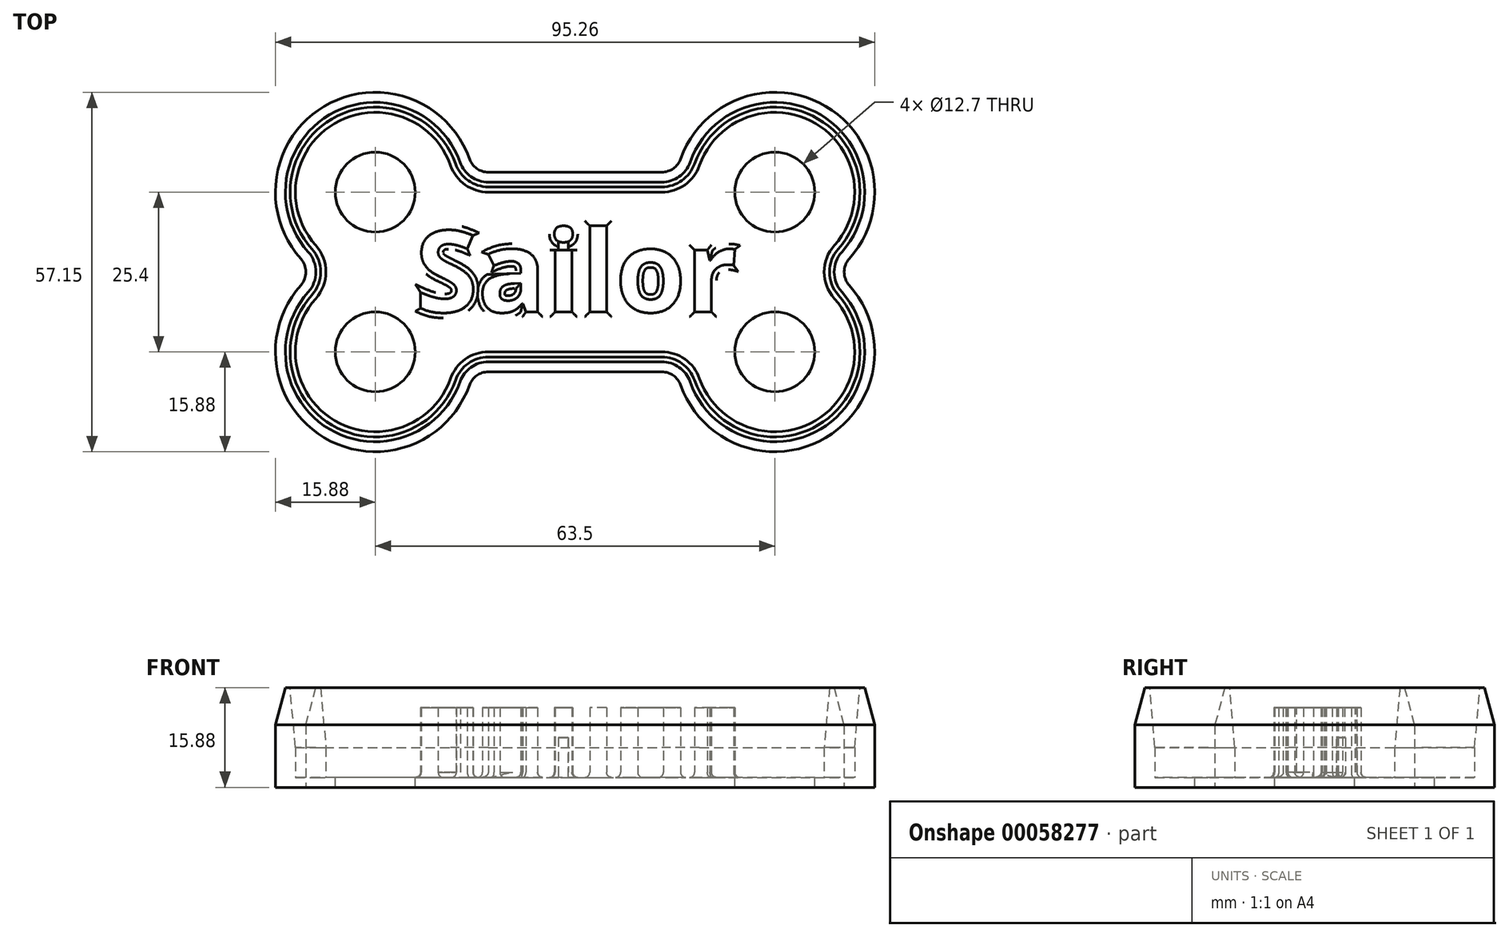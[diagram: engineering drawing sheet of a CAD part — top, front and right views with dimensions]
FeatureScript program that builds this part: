
annotation { "Feature Type Name" : "Feature", "Feature Type Description" : "" }
export const myFeature = defineFeature(function(context is Context, id is Id, definition is map)
    precondition{}
    {
        {
            var Q0;
            Q0=qCreatedBy(makeId("Top.planeOp"),FACE);
            var sketch = newSketch(context, id + "F0", { "sketchPlane" : qUnion([Q0])});
            skText(sketch, "E0", { "text": "Sailor", "fontName": "OpenSans-Bold.ttf"});
            const initialGuessF0  = {"E0": [0, 0, 1, 0, 0.01298]};
            skSetInitialGuess(sketch, initialGuessF0);
            skSolve(sketch);
        }
        {
            var Q0;
            Q0=qSketchRegion(id+"F0",true);
            extrude(context, id + "F1", {"entities" : qUnion([Q0]), "depth" : 12.7 * mm});
        }
        {
            var Q0;
            Q0=qCreatedBy(makeId("Top.planeOp"),FACE);
            var sketch = newSketch(context, id + "F2", { "sketchPlane" : qUnion([Q0])});
            skLineSegment(sketch, "E1.bottom", {"start": v(11.61, 19.05) * mm, "end": v(39.19, 19.05) * mm});
            skLineSegment(sketch, "E1.top", {"start": v(11.61, -6.35) * mm, "end": v(39.19, -6.35) * mm});
            skArc(sketch, "E2", {"start": v(5.62, 23.28) * mm, "mid": v(-12.82, 29.98) * mm, "end": v(-15.82, 10.58) * mm});
            skArc(sketch, "E3", {"start": v(-15.82, 2.12) * mm, "mid": v(-12.82, -17.28) * mm, "end": v(5.62, -10.58) * mm});
            skArc(sketch, "E4", {"start": v(66.62, 10.58) * mm, "mid": v(63.62, 29.98) * mm, "end": v(45.18, 23.28) * mm});
            skArc(sketch, "E5", {"start": v(45.18, -10.58) * mm, "mid": v(63.62, -17.28) * mm, "end": v(66.62, 2.12) * mm});
            skPoint(sketch, "E6.visualSharp", {"position": v(-6.35, 6.35) * mm});
            skArc(sketch, "E6.filletArc", {"start": v(-15.82, 2.12) * mm, "mid": v(-14.2, 6.35) * mm, "end": v(-15.82, 10.58) * mm});
            skPoint(sketch, "E7.visualSharp", {"position": v(57.15, 6.35) * mm});
            skArc(sketch, "E7.filletArc", {"start": v(66.62, 10.58) * mm, "mid": v(65, 6.35) * mm, "end": v(66.62, 2.12) * mm});
            skPoint(sketch, "E8.visualSharp", {"position": v(44.45, 19.05) * mm});
            skArc(sketch, "E8.filletArc", {"start": v(39.19, 19.05) * mm, "mid": v(42.86, 20.22) * mm, "end": v(45.18, 23.28) * mm});
            skPoint(sketch, "E9.visualSharp", {"position": v(6.35, 19.05) * mm});
            skArc(sketch, "E9.filletArc", {"start": v(5.62, 23.28) * mm, "mid": v(7.94, 20.22) * mm, "end": v(11.61, 19.05) * mm});
            skPoint(sketch, "E10.visualSharp", {"position": v(6.35, -6.35) * mm});
            skArc(sketch, "E10.filletArc", {"start": v(11.61, -6.35) * mm, "mid": v(7.94, -7.52) * mm, "end": v(5.62, -10.58) * mm});
            skPoint(sketch, "E11.visualSharp", {"position": v(44.45, -6.35) * mm});
            skArc(sketch, "E11.filletArc", {"start": v(45.18, -10.58) * mm, "mid": v(42.86, -7.52) * mm, "end": v(39.19, -6.35) * mm});
            skArc(sketch, "E12.0", {"start": v(8.62, 24.34) * mm, "mid": v(9.78, 22.8) * mm, "end": v(11.61, 22.23) * mm});
            skArc(sketch, "E12.1", {"start": v(42.18, -11.64) * mm, "mid": v(65.24, -20) * mm, "end": v(68.98, 4.23) * mm});
            skArc(sketch, "E12.2", {"start": v(68.98, 8.47) * mm, "mid": v(68.17, 6.35) * mm, "end": v(68.98, 4.23) * mm});
            skArc(sketch, "E12.3", {"start": v(68.98, 8.47) * mm, "mid": v(65.24, 32.7) * mm, "end": v(42.18, 24.34) * mm});
            skArc(sketch, "E12.4", {"start": v(39.19, 22.23) * mm, "mid": v(41.02, 22.8) * mm, "end": v(42.18, 24.34) * mm});
            skArc(sketch, "E12.5", {"start": v(42.18, -11.64) * mm, "mid": v(41.02, -10.1) * mm, "end": v(39.19, -9.52) * mm});
            skLineSegment(sketch, "E12.6", {"start": v(11.61, 22.22) * mm, "end": v(39.19, 22.23) * mm});
            skLineSegment(sketch, "E12.7", {"start": v(11.61, -9.53) * mm, "end": v(39.19, -9.52) * mm});
            skArc(sketch, "E12.8", {"start": v(11.61, -9.53) * mm, "mid": v(9.78, -10.1) * mm, "end": v(8.62, -11.64) * mm});
            skArc(sketch, "E12.9", {"start": v(-18.18, 4.23) * mm, "mid": v(-14.44, -20) * mm, "end": v(8.62, -11.64) * mm});
            skArc(sketch, "E12.10", {"start": v(-18.18, 4.23) * mm, "mid": v(-17.37, 6.35) * mm, "end": v(-18.18, 8.47) * mm});
            skArc(sketch, "E12.11", {"start": v(8.62, 24.34) * mm, "mid": v(-14.44, 32.7) * mm, "end": v(-18.18, 8.47) * mm});
            skSolve(sketch);
        }
        {
            var Q0;
            Q0=qSketchRegion(id+"F2",true);
            extrude(context, id + "F3", {"entities" : qUnion([Q0]), "depth" : 15.88 * mm});
        }
        {
            var Q0;
            Q0=makeQuery(id+"F3.opExtrude","CAP_EDGE",EDGE,{"disambiguationData":[OSD([sQuery(id+"F2.wireOp",EDGE,"E2")])],"isStart":false});
            chamfer(context, id + "F4", {"entities" : qUnion([Q0]), "chamferType" : ChamferType.OFFSET_ANGLE, "width" : 9.52 * mm, "oppositeDirection" : false, "angle" : 5 * degree, "tangentPropagation" : true});
        }
        {
            var Q0;
            Q0=makeQuery(id+"F3.opExtrude","CAP_EDGE",EDGE,{"disambiguationData":[OSD([sQuery(id+"F2.wireOp",EDGE,"E12.11")])],"isStart":false});
            chamfer(context, id + "F5", {"entities" : qUnion([Q0]), "chamferType" : ChamferType.OFFSET_ANGLE, "width" : 1.59 * mm, "oppositeDirection" : false, "angle" : 75 * degree, "tangentPropagation" : true});
        }
        {
            var Q0;
            Q0=qCreatedBy(makeId("Top.planeOp"),FACE);
            var sketch = newSketch(context, id + "F6", { "sketchPlane" : qUnion([Q0])});
            skArc(sketch, "E13.0", {"start": v(-18.18, 8.47) * mm, "mid": v(-14.44, 32.7) * mm, "end": v(8.62, 24.34) * mm});
            skArc(sketch, "E14.0", {"start": v(8.62, 24.34) * mm, "mid": v(9.78, 22.8) * mm, "end": v(11.61, 22.23) * mm});
            skLineSegment(sketch, "E15.0", {"start": v(11.61, 22.22) * mm, "end": v(39.19, 22.23) * mm});
            skArc(sketch, "E16.0", {"start": v(39.19, 22.23) * mm, "mid": v(41.02, 22.8) * mm, "end": v(42.18, 24.34) * mm});
            skArc(sketch, "E17.0", {"start": v(42.18, 24.34) * mm, "mid": v(65.24, 32.7) * mm, "end": v(68.98, 8.47) * mm});
            skArc(sketch, "E18.0", {"start": v(68.98, 8.47) * mm, "mid": v(68.17, 6.35) * mm, "end": v(68.98, 4.23) * mm});
            skArc(sketch, "E19.0", {"start": v(68.98, 4.23) * mm, "mid": v(65.24, -20) * mm, "end": v(42.18, -11.64) * mm});
            skArc(sketch, "E20.0", {"start": v(42.18, -11.64) * mm, "mid": v(41.02, -10.1) * mm, "end": v(39.19, -9.52) * mm});
            skLineSegment(sketch, "E21.0", {"start": v(39.19, -9.52) * mm, "end": v(11.61, -9.53) * mm});
            skArc(sketch, "E22.0", {"start": v(11.61, -9.53) * mm, "mid": v(9.78, -10.1) * mm, "end": v(8.62, -11.64) * mm});
            skArc(sketch, "E23.0", {"start": v(8.62, -11.64) * mm, "mid": v(-14.44, -20) * mm, "end": v(-18.18, 4.23) * mm});
            skArc(sketch, "E24.0", {"start": v(-18.18, 4.23) * mm, "mid": v(-17.37, 6.35) * mm, "end": v(-18.18, 8.47) * mm});
            skSolve(sketch);
        }
        {
            var Q0;
            Q0=qSketchRegion(id+"F6",true);
            extrude(context, id + "F7", {"entities" : qUnion([Q0]), "operationType" : NewBodyOperationType.ADD, "depth" : 1.59 * mm});
        }
        {
            var Q0;
            Q0=makeQuery(id+"F7.boolean.opBoolean","SPLIT",FACE,{"disambiguationData":[TD([makeQuery(id+"F1.opExtrude","SWEPT_FACE",FACE,{"disambiguationData":[OSD([sQuery(id+"F0.wireOp",EDGE,"E0.sketch_text.stroke-0")])]})])],"derivedFrom":makeQuery(id+"F7.opExtrude","CAP_FACE",FACE,{"disambiguationData":[OSD([sQuery(id+"F6.wireOp",EDGE,"E13.0"),sQuery(id+"F6.wireOp",EDGE,"E14.0"),sQuery(id+"F6.wireOp",EDGE,"E15.0"),sQuery(id+"F6.wireOp",EDGE,"E16.0"),sQuery(id+"F6.wireOp",EDGE,"E17.0"),sQuery(id+"F6.wireOp",EDGE,"E18.0"),sQuery(id+"F6.wireOp",EDGE,"E19.0"),sQuery(id+"F6.wireOp",EDGE,"E20.0"),sQuery(id+"F6.wireOp",EDGE,"E21.0"),sQuery(id+"F6.wireOp",EDGE,"E22.0"),sQuery(id+"F6.wireOp",EDGE,"E23.0"),sQuery(id+"F6.wireOp",EDGE,"E24.0")])],"isStart":false})});
            var sketch = newSketch(context, id + "F8", { "sketchPlane" : qUnion([Q0])});
            skLineSegment(sketch, "E25", {"start": v(22.73, 11.85) * mm, "end": v(22.73, 9.14) * mm});
            skLineSegment(sketch, "E26", {"start": v(22.73, 9.14) * mm, "end": v(24.32, 9.14) * mm});
            skLineSegment(sketch, "E27", {"start": v(24.32, 9.14) * mm, "end": v(24.32, 11.85) * mm});
            skLineSegment(sketch, "E28", {"start": v(24.32, 11.85) * mm, "end": v(22.73, 11.85) * mm});
            skSolve(sketch);
        }
        {
            var Q0;
            Q0=qSketchRegion(id+"F8",true);
            extrude(context, id + "F9", {"entities" : qUnion([Q0]), "operationType" : NewBodyOperationType.ADD, "depth" : 6.35 * mm});
        }
        {
            var Q0;
            Q0=makeQuery(id+"F7.boolean.opBoolean","INTERSECT",EDGE,{"derivedFrom":[makeQuery(id+"F1.opExtrude","SWEPT_FACE",FACE,{"disambiguationData":[OSD([sQuery(id+"F0.wireOp",EDGE,"E0.sketch_text.stroke-14")])]}),makeQuery(id+"F7.opExtrude","CAP_FACE",FACE,{"disambiguationData":[OSD([sQuery(id+"F6.wireOp",EDGE,"E13.0"),sQuery(id+"F6.wireOp",EDGE,"E14.0"),sQuery(id+"F6.wireOp",EDGE,"E15.0"),sQuery(id+"F6.wireOp",EDGE,"E16.0"),sQuery(id+"F6.wireOp",EDGE,"E17.0"),sQuery(id+"F6.wireOp",EDGE,"E18.0"),sQuery(id+"F6.wireOp",EDGE,"E19.0"),sQuery(id+"F6.wireOp",EDGE,"E20.0"),sQuery(id+"F6.wireOp",EDGE,"E21.0"),sQuery(id+"F6.wireOp",EDGE,"E22.0"),sQuery(id+"F6.wireOp",EDGE,"E23.0"),sQuery(id+"F6.wireOp",EDGE,"E24.0")])],"isStart":false})]});
            var Q1;
            Q1=makeQuery(id+"F7.boolean.opBoolean","INTERSECT",EDGE,{"derivedFrom":[makeQuery(id+"F1.opExtrude","SWEPT_FACE",FACE,{"disambiguationData":[OSD([sQuery(id+"F0.wireOp",EDGE,"E0.sketch_text.stroke-7")])]}),makeQuery(id+"F7.opExtrude","CAP_FACE",FACE,{"disambiguationData":[OSD([sQuery(id+"F6.wireOp",EDGE,"E13.0"),sQuery(id+"F6.wireOp",EDGE,"E14.0"),sQuery(id+"F6.wireOp",EDGE,"E15.0"),sQuery(id+"F6.wireOp",EDGE,"E16.0"),sQuery(id+"F6.wireOp",EDGE,"E17.0"),sQuery(id+"F6.wireOp",EDGE,"E18.0"),sQuery(id+"F6.wireOp",EDGE,"E19.0"),sQuery(id+"F6.wireOp",EDGE,"E20.0"),sQuery(id+"F6.wireOp",EDGE,"E21.0"),sQuery(id+"F6.wireOp",EDGE,"E22.0"),sQuery(id+"F6.wireOp",EDGE,"E23.0"),sQuery(id+"F6.wireOp",EDGE,"E24.0")])],"isStart":false})]});
            var Q2;
            Q2=makeQuery(id+"F7.boolean.opBoolean","INTERSECT",EDGE,{"derivedFrom":[makeQuery(id+"F1.opExtrude","SWEPT_FACE",FACE,{"disambiguationData":[OSD([sQuery(id+"F0.wireOp",EDGE,"E0.sketch_text.stroke-3")])]}),makeQuery(id+"F7.opExtrude","CAP_FACE",FACE,{"disambiguationData":[OSD([sQuery(id+"F6.wireOp",EDGE,"E13.0"),sQuery(id+"F6.wireOp",EDGE,"E14.0"),sQuery(id+"F6.wireOp",EDGE,"E15.0"),sQuery(id+"F6.wireOp",EDGE,"E16.0"),sQuery(id+"F6.wireOp",EDGE,"E17.0"),sQuery(id+"F6.wireOp",EDGE,"E18.0"),sQuery(id+"F6.wireOp",EDGE,"E19.0"),sQuery(id+"F6.wireOp",EDGE,"E20.0"),sQuery(id+"F6.wireOp",EDGE,"E21.0"),sQuery(id+"F6.wireOp",EDGE,"E22.0"),sQuery(id+"F6.wireOp",EDGE,"E23.0"),sQuery(id+"F6.wireOp",EDGE,"E24.0")])],"isStart":false})]});
            var Q3;
            Q3=makeQuery(id+"F7.boolean.opBoolean","INTERSECT",EDGE,{"derivedFrom":[makeQuery(id+"F1.opExtrude","SWEPT_FACE",FACE,{"disambiguationData":[OSD([sQuery(id+"F0.wireOp",EDGE,"E0.sketch_text.stroke-1")])]}),makeQuery(id+"F7.opExtrude","CAP_FACE",FACE,{"disambiguationData":[OSD([sQuery(id+"F6.wireOp",EDGE,"E13.0"),sQuery(id+"F6.wireOp",EDGE,"E14.0"),sQuery(id+"F6.wireOp",EDGE,"E15.0"),sQuery(id+"F6.wireOp",EDGE,"E16.0"),sQuery(id+"F6.wireOp",EDGE,"E17.0"),sQuery(id+"F6.wireOp",EDGE,"E18.0"),sQuery(id+"F6.wireOp",EDGE,"E19.0"),sQuery(id+"F6.wireOp",EDGE,"E20.0"),sQuery(id+"F6.wireOp",EDGE,"E21.0"),sQuery(id+"F6.wireOp",EDGE,"E22.0"),sQuery(id+"F6.wireOp",EDGE,"E23.0"),sQuery(id+"F6.wireOp",EDGE,"E24.0")])],"isStart":false})]});
            var Q4;
            Q4=makeQuery(id+"F7.boolean.opBoolean","INTERSECT",EDGE,{"derivedFrom":[makeQuery(id+"F1.opExtrude","SWEPT_FACE",FACE,{"disambiguationData":[OSD([sQuery(id+"F0.wireOp",EDGE,"E0.sketch_text.stroke-20")])]}),makeQuery(id+"F7.opExtrude","CAP_FACE",FACE,{"disambiguationData":[OSD([sQuery(id+"F6.wireOp",EDGE,"E13.0"),sQuery(id+"F6.wireOp",EDGE,"E14.0"),sQuery(id+"F6.wireOp",EDGE,"E15.0"),sQuery(id+"F6.wireOp",EDGE,"E16.0"),sQuery(id+"F6.wireOp",EDGE,"E17.0"),sQuery(id+"F6.wireOp",EDGE,"E18.0"),sQuery(id+"F6.wireOp",EDGE,"E19.0"),sQuery(id+"F6.wireOp",EDGE,"E20.0"),sQuery(id+"F6.wireOp",EDGE,"E21.0"),sQuery(id+"F6.wireOp",EDGE,"E22.0"),sQuery(id+"F6.wireOp",EDGE,"E23.0"),sQuery(id+"F6.wireOp",EDGE,"E24.0")])],"isStart":false})]});
            var Q5;
            Q5=makeQuery(id+"F7.boolean.opBoolean","INTERSECT",EDGE,{"derivedFrom":[makeQuery(id+"F1.opExtrude","SWEPT_FACE",FACE,{"disambiguationData":[OSD([sQuery(id+"F0.wireOp",EDGE,"E0.sketch_text.stroke-18")])]}),makeQuery(id+"F7.opExtrude","CAP_FACE",FACE,{"disambiguationData":[OSD([sQuery(id+"F6.wireOp",EDGE,"E13.0"),sQuery(id+"F6.wireOp",EDGE,"E14.0"),sQuery(id+"F6.wireOp",EDGE,"E15.0"),sQuery(id+"F6.wireOp",EDGE,"E16.0"),sQuery(id+"F6.wireOp",EDGE,"E17.0"),sQuery(id+"F6.wireOp",EDGE,"E18.0"),sQuery(id+"F6.wireOp",EDGE,"E19.0"),sQuery(id+"F6.wireOp",EDGE,"E20.0"),sQuery(id+"F6.wireOp",EDGE,"E21.0"),sQuery(id+"F6.wireOp",EDGE,"E22.0"),sQuery(id+"F6.wireOp",EDGE,"E23.0"),sQuery(id+"F6.wireOp",EDGE,"E24.0")])],"isStart":false})]});
            var Q6;
            Q6=makeQuery(id+"F7.boolean.opBoolean","INTERSECT",EDGE,{"derivedFrom":[makeQuery(id+"F1.opExtrude","SWEPT_FACE",FACE,{"disambiguationData":[OSD([sQuery(id+"F0.wireOp",EDGE,"E0.sketch_text.stroke-32")])]}),makeQuery(id+"F7.opExtrude","CAP_FACE",FACE,{"disambiguationData":[OSD([sQuery(id+"F6.wireOp",EDGE,"E13.0"),sQuery(id+"F6.wireOp",EDGE,"E14.0"),sQuery(id+"F6.wireOp",EDGE,"E15.0"),sQuery(id+"F6.wireOp",EDGE,"E16.0"),sQuery(id+"F6.wireOp",EDGE,"E17.0"),sQuery(id+"F6.wireOp",EDGE,"E18.0"),sQuery(id+"F6.wireOp",EDGE,"E19.0"),sQuery(id+"F6.wireOp",EDGE,"E20.0"),sQuery(id+"F6.wireOp",EDGE,"E21.0"),sQuery(id+"F6.wireOp",EDGE,"E22.0"),sQuery(id+"F6.wireOp",EDGE,"E23.0"),sQuery(id+"F6.wireOp",EDGE,"E24.0")])],"isStart":false})]});
            var Q7;
            Q7=makeQuery(id+"F7.boolean.opBoolean","INTERSECT",EDGE,{"derivedFrom":[makeQuery(id+"F1.opExtrude","SWEPT_FACE",FACE,{"disambiguationData":[OSD([sQuery(id+"F0.wireOp",EDGE,"E0.sketch_text.stroke-28")])]}),makeQuery(id+"F7.opExtrude","CAP_FACE",FACE,{"disambiguationData":[OSD([sQuery(id+"F6.wireOp",EDGE,"E13.0"),sQuery(id+"F6.wireOp",EDGE,"E14.0"),sQuery(id+"F6.wireOp",EDGE,"E15.0"),sQuery(id+"F6.wireOp",EDGE,"E16.0"),sQuery(id+"F6.wireOp",EDGE,"E17.0"),sQuery(id+"F6.wireOp",EDGE,"E18.0"),sQuery(id+"F6.wireOp",EDGE,"E19.0"),sQuery(id+"F6.wireOp",EDGE,"E20.0"),sQuery(id+"F6.wireOp",EDGE,"E21.0"),sQuery(id+"F6.wireOp",EDGE,"E22.0"),sQuery(id+"F6.wireOp",EDGE,"E23.0"),sQuery(id+"F6.wireOp",EDGE,"E24.0")])],"isStart":false})]});
            var Q8;
            Q8=makeQuery(id+"F7.boolean.opBoolean","INTERSECT",EDGE,{"derivedFrom":[makeQuery(id+"F1.opExtrude","SWEPT_FACE",FACE,{"disambiguationData":[OSD([sQuery(id+"F0.wireOp",EDGE,"E0.sketch_text.stroke-45")])]}),makeQuery(id+"F7.opExtrude","CAP_FACE",FACE,{"disambiguationData":[OSD([sQuery(id+"F6.wireOp",EDGE,"E13.0"),sQuery(id+"F6.wireOp",EDGE,"E14.0"),sQuery(id+"F6.wireOp",EDGE,"E15.0"),sQuery(id+"F6.wireOp",EDGE,"E16.0"),sQuery(id+"F6.wireOp",EDGE,"E17.0"),sQuery(id+"F6.wireOp",EDGE,"E18.0"),sQuery(id+"F6.wireOp",EDGE,"E19.0"),sQuery(id+"F6.wireOp",EDGE,"E20.0"),sQuery(id+"F6.wireOp",EDGE,"E21.0"),sQuery(id+"F6.wireOp",EDGE,"E22.0"),sQuery(id+"F6.wireOp",EDGE,"E23.0"),sQuery(id+"F6.wireOp",EDGE,"E24.0")])],"isStart":false})]});
            var Q9;
            Q9=makeQuery(id+"F7.boolean.opBoolean","INTERSECT",EDGE,{"derivedFrom":[makeQuery(id+"F1.opExtrude","SWEPT_FACE",FACE,{"disambiguationData":[OSD([sQuery(id+"F0.wireOp",EDGE,"E0.sketch_text.stroke-44")])]}),makeQuery(id+"F7.opExtrude","CAP_FACE",FACE,{"disambiguationData":[OSD([sQuery(id+"F6.wireOp",EDGE,"E13.0"),sQuery(id+"F6.wireOp",EDGE,"E14.0"),sQuery(id+"F6.wireOp",EDGE,"E15.0"),sQuery(id+"F6.wireOp",EDGE,"E16.0"),sQuery(id+"F6.wireOp",EDGE,"E17.0"),sQuery(id+"F6.wireOp",EDGE,"E18.0"),sQuery(id+"F6.wireOp",EDGE,"E19.0"),sQuery(id+"F6.wireOp",EDGE,"E20.0"),sQuery(id+"F6.wireOp",EDGE,"E21.0"),sQuery(id+"F6.wireOp",EDGE,"E22.0"),sQuery(id+"F6.wireOp",EDGE,"E23.0"),sQuery(id+"F6.wireOp",EDGE,"E24.0")])],"isStart":false})]});
            var Q10;
            Q10=makeQuery(id+"F7.boolean.opBoolean","INTERSECT",EDGE,{"derivedFrom":[makeQuery(id+"F1.opExtrude","SWEPT_FACE",FACE,{"disambiguationData":[OSD([sQuery(id+"F0.wireOp",EDGE,"E0.sketch_text.stroke-40")])]}),makeQuery(id+"F7.opExtrude","CAP_FACE",FACE,{"disambiguationData":[OSD([sQuery(id+"F6.wireOp",EDGE,"E13.0"),sQuery(id+"F6.wireOp",EDGE,"E14.0"),sQuery(id+"F6.wireOp",EDGE,"E15.0"),sQuery(id+"F6.wireOp",EDGE,"E16.0"),sQuery(id+"F6.wireOp",EDGE,"E17.0"),sQuery(id+"F6.wireOp",EDGE,"E18.0"),sQuery(id+"F6.wireOp",EDGE,"E19.0"),sQuery(id+"F6.wireOp",EDGE,"E20.0"),sQuery(id+"F6.wireOp",EDGE,"E21.0"),sQuery(id+"F6.wireOp",EDGE,"E22.0"),sQuery(id+"F6.wireOp",EDGE,"E23.0"),sQuery(id+"F6.wireOp",EDGE,"E24.0")])],"isStart":false})]});
            var Q11;
            Q11=makeQuery(id+"F7.boolean.opBoolean","INTERSECT",EDGE,{"derivedFrom":[makeQuery(id+"F1.opExtrude","SWEPT_FACE",FACE,{"disambiguationData":[OSD([sQuery(id+"F0.wireOp",EDGE,"E0.sketch_text.stroke-39")])]}),makeQuery(id+"F7.opExtrude","CAP_FACE",FACE,{"disambiguationData":[OSD([sQuery(id+"F6.wireOp",EDGE,"E13.0"),sQuery(id+"F6.wireOp",EDGE,"E14.0"),sQuery(id+"F6.wireOp",EDGE,"E15.0"),sQuery(id+"F6.wireOp",EDGE,"E16.0"),sQuery(id+"F6.wireOp",EDGE,"E17.0"),sQuery(id+"F6.wireOp",EDGE,"E18.0"),sQuery(id+"F6.wireOp",EDGE,"E19.0"),sQuery(id+"F6.wireOp",EDGE,"E20.0"),sQuery(id+"F6.wireOp",EDGE,"E21.0"),sQuery(id+"F6.wireOp",EDGE,"E22.0"),sQuery(id+"F6.wireOp",EDGE,"E23.0"),sQuery(id+"F6.wireOp",EDGE,"E24.0")])],"isStart":false})]});
            var Q12;
            Q12=makeQuery(id+"F7.boolean.opBoolean","INTERSECT",EDGE,{"derivedFrom":[makeQuery(id+"F1.opExtrude","SWEPT_FACE",FACE,{"disambiguationData":[OSD([sQuery(id+"F0.wireOp",EDGE,"E0.sketch_text.stroke-52")])]}),makeQuery(id+"F7.opExtrude","CAP_FACE",FACE,{"disambiguationData":[OSD([sQuery(id+"F6.wireOp",EDGE,"E13.0"),sQuery(id+"F6.wireOp",EDGE,"E14.0"),sQuery(id+"F6.wireOp",EDGE,"E15.0"),sQuery(id+"F6.wireOp",EDGE,"E16.0"),sQuery(id+"F6.wireOp",EDGE,"E17.0"),sQuery(id+"F6.wireOp",EDGE,"E18.0"),sQuery(id+"F6.wireOp",EDGE,"E19.0"),sQuery(id+"F6.wireOp",EDGE,"E20.0"),sQuery(id+"F6.wireOp",EDGE,"E21.0"),sQuery(id+"F6.wireOp",EDGE,"E22.0"),sQuery(id+"F6.wireOp",EDGE,"E23.0"),sQuery(id+"F6.wireOp",EDGE,"E24.0")])],"isStart":false})]});
            var Q13;
            Q13=makeQuery(id+"F7.boolean.opBoolean","INTERSECT",EDGE,{"derivedFrom":[makeQuery(id+"F1.opExtrude","SWEPT_FACE",FACE,{"disambiguationData":[OSD([sQuery(id+"F0.wireOp",EDGE,"E0.sketch_text.stroke-59")])]}),makeQuery(id+"F7.opExtrude","CAP_FACE",FACE,{"disambiguationData":[OSD([sQuery(id+"F6.wireOp",EDGE,"E13.0"),sQuery(id+"F6.wireOp",EDGE,"E14.0"),sQuery(id+"F6.wireOp",EDGE,"E15.0"),sQuery(id+"F6.wireOp",EDGE,"E16.0"),sQuery(id+"F6.wireOp",EDGE,"E17.0"),sQuery(id+"F6.wireOp",EDGE,"E18.0"),sQuery(id+"F6.wireOp",EDGE,"E19.0"),sQuery(id+"F6.wireOp",EDGE,"E20.0"),sQuery(id+"F6.wireOp",EDGE,"E21.0"),sQuery(id+"F6.wireOp",EDGE,"E22.0"),sQuery(id+"F6.wireOp",EDGE,"E23.0"),sQuery(id+"F6.wireOp",EDGE,"E24.0")])],"isStart":false})]});
            var Q14;
            Q14=makeQuery(id+"F7.boolean.opBoolean","INTERSECT",EDGE,{"derivedFrom":[makeQuery(id+"F1.opExtrude","SWEPT_FACE",FACE,{"disambiguationData":[OSD([sQuery(id+"F0.wireOp",EDGE,"E0.sketch_text.stroke-58")])]}),makeQuery(id+"F7.opExtrude","CAP_FACE",FACE,{"disambiguationData":[OSD([sQuery(id+"F6.wireOp",EDGE,"E13.0"),sQuery(id+"F6.wireOp",EDGE,"E14.0"),sQuery(id+"F6.wireOp",EDGE,"E15.0"),sQuery(id+"F6.wireOp",EDGE,"E16.0"),sQuery(id+"F6.wireOp",EDGE,"E17.0"),sQuery(id+"F6.wireOp",EDGE,"E18.0"),sQuery(id+"F6.wireOp",EDGE,"E19.0"),sQuery(id+"F6.wireOp",EDGE,"E20.0"),sQuery(id+"F6.wireOp",EDGE,"E21.0"),sQuery(id+"F6.wireOp",EDGE,"E22.0"),sQuery(id+"F6.wireOp",EDGE,"E23.0"),sQuery(id+"F6.wireOp",EDGE,"E24.0")])],"isStart":false})]});
            var Q15;
            Q15=makeQuery(id+"F7.boolean.opBoolean","INTERSECT",EDGE,{"derivedFrom":[makeQuery(id+"F1.opExtrude","SWEPT_FACE",FACE,{"disambiguationData":[OSD([sQuery(id+"F0.wireOp",EDGE,"E0.sketch_text.stroke-61")])]}),makeQuery(id+"F7.opExtrude","CAP_FACE",FACE,{"disambiguationData":[OSD([sQuery(id+"F6.wireOp",EDGE,"E13.0"),sQuery(id+"F6.wireOp",EDGE,"E14.0"),sQuery(id+"F6.wireOp",EDGE,"E15.0"),sQuery(id+"F6.wireOp",EDGE,"E16.0"),sQuery(id+"F6.wireOp",EDGE,"E17.0"),sQuery(id+"F6.wireOp",EDGE,"E18.0"),sQuery(id+"F6.wireOp",EDGE,"E19.0"),sQuery(id+"F6.wireOp",EDGE,"E20.0"),sQuery(id+"F6.wireOp",EDGE,"E21.0"),sQuery(id+"F6.wireOp",EDGE,"E22.0"),sQuery(id+"F6.wireOp",EDGE,"E23.0"),sQuery(id+"F6.wireOp",EDGE,"E24.0")])],"isStart":false})]});
            var Q16;
            Q16=makeQuery(id+"F7.boolean.opBoolean","INTERSECT",EDGE,{"derivedFrom":[makeQuery(id+"F1.opExtrude","SWEPT_FACE",FACE,{"disambiguationData":[OSD([sQuery(id+"F0.wireOp",EDGE,"E0.sketch_text.stroke-62")])]}),makeQuery(id+"F7.opExtrude","CAP_FACE",FACE,{"disambiguationData":[OSD([sQuery(id+"F6.wireOp",EDGE,"E13.0"),sQuery(id+"F6.wireOp",EDGE,"E14.0"),sQuery(id+"F6.wireOp",EDGE,"E15.0"),sQuery(id+"F6.wireOp",EDGE,"E16.0"),sQuery(id+"F6.wireOp",EDGE,"E17.0"),sQuery(id+"F6.wireOp",EDGE,"E18.0"),sQuery(id+"F6.wireOp",EDGE,"E19.0"),sQuery(id+"F6.wireOp",EDGE,"E20.0"),sQuery(id+"F6.wireOp",EDGE,"E21.0"),sQuery(id+"F6.wireOp",EDGE,"E22.0"),sQuery(id+"F6.wireOp",EDGE,"E23.0"),sQuery(id+"F6.wireOp",EDGE,"E24.0")])],"isStart":false})]});
            var Q17;
            Q17=makeQuery(id+"F7.boolean.opBoolean","INTERSECT",EDGE,{"derivedFrom":[makeQuery(id+"F1.opExtrude","SWEPT_FACE",FACE,{"disambiguationData":[OSD([sQuery(id+"F0.wireOp",EDGE,"E0.sketch_text.stroke-65")])]}),makeQuery(id+"F7.opExtrude","CAP_FACE",FACE,{"disambiguationData":[OSD([sQuery(id+"F6.wireOp",EDGE,"E13.0"),sQuery(id+"F6.wireOp",EDGE,"E14.0"),sQuery(id+"F6.wireOp",EDGE,"E15.0"),sQuery(id+"F6.wireOp",EDGE,"E16.0"),sQuery(id+"F6.wireOp",EDGE,"E17.0"),sQuery(id+"F6.wireOp",EDGE,"E18.0"),sQuery(id+"F6.wireOp",EDGE,"E19.0"),sQuery(id+"F6.wireOp",EDGE,"E20.0"),sQuery(id+"F6.wireOp",EDGE,"E21.0"),sQuery(id+"F6.wireOp",EDGE,"E22.0"),sQuery(id+"F6.wireOp",EDGE,"E23.0"),sQuery(id+"F6.wireOp",EDGE,"E24.0")])],"isStart":false})]});
            var Q18;
            Q18=makeQuery(id+"F7.boolean.opBoolean","INTERSECT",EDGE,{"derivedFrom":[makeQuery(id+"F1.opExtrude","SWEPT_FACE",FACE,{"disambiguationData":[OSD([sQuery(id+"F0.wireOp",EDGE,"E0.sketch_text.stroke-55")])]}),makeQuery(id+"F7.opExtrude","CAP_FACE",FACE,{"disambiguationData":[OSD([sQuery(id+"F6.wireOp",EDGE,"E13.0"),sQuery(id+"F6.wireOp",EDGE,"E14.0"),sQuery(id+"F6.wireOp",EDGE,"E15.0"),sQuery(id+"F6.wireOp",EDGE,"E16.0"),sQuery(id+"F6.wireOp",EDGE,"E17.0"),sQuery(id+"F6.wireOp",EDGE,"E18.0"),sQuery(id+"F6.wireOp",EDGE,"E19.0"),sQuery(id+"F6.wireOp",EDGE,"E20.0"),sQuery(id+"F6.wireOp",EDGE,"E21.0"),sQuery(id+"F6.wireOp",EDGE,"E22.0"),sQuery(id+"F6.wireOp",EDGE,"E23.0"),sQuery(id+"F6.wireOp",EDGE,"E24.0")])],"isStart":false})]});
            var Q19;
            Q19=makeQuery(id+"F7.boolean.opBoolean","INTERSECT",EDGE,{"derivedFrom":[makeQuery(id+"F1.opExtrude","SWEPT_FACE",FACE,{"disambiguationData":[OSD([sQuery(id+"F0.wireOp",EDGE,"E0.sketch_text.stroke-63")])]}),makeQuery(id+"F7.opExtrude","CAP_FACE",FACE,{"disambiguationData":[OSD([sQuery(id+"F6.wireOp",EDGE,"E13.0"),sQuery(id+"F6.wireOp",EDGE,"E14.0"),sQuery(id+"F6.wireOp",EDGE,"E15.0"),sQuery(id+"F6.wireOp",EDGE,"E16.0"),sQuery(id+"F6.wireOp",EDGE,"E17.0"),sQuery(id+"F6.wireOp",EDGE,"E18.0"),sQuery(id+"F6.wireOp",EDGE,"E19.0"),sQuery(id+"F6.wireOp",EDGE,"E20.0"),sQuery(id+"F6.wireOp",EDGE,"E21.0"),sQuery(id+"F6.wireOp",EDGE,"E22.0"),sQuery(id+"F6.wireOp",EDGE,"E23.0"),sQuery(id+"F6.wireOp",EDGE,"E24.0")])],"isStart":false})]});
            var Q20;
            Q20=makeQuery(id+"F7.boolean.opBoolean","INTERSECT",EDGE,{"derivedFrom":[makeQuery(id+"F1.opExtrude","SWEPT_FACE",FACE,{"disambiguationData":[OSD([sQuery(id+"F0.wireOp",EDGE,"E0.sketch_text.stroke-64")])]}),makeQuery(id+"F7.opExtrude","CAP_FACE",FACE,{"disambiguationData":[OSD([sQuery(id+"F6.wireOp",EDGE,"E13.0"),sQuery(id+"F6.wireOp",EDGE,"E14.0"),sQuery(id+"F6.wireOp",EDGE,"E15.0"),sQuery(id+"F6.wireOp",EDGE,"E16.0"),sQuery(id+"F6.wireOp",EDGE,"E17.0"),sQuery(id+"F6.wireOp",EDGE,"E18.0"),sQuery(id+"F6.wireOp",EDGE,"E19.0"),sQuery(id+"F6.wireOp",EDGE,"E20.0"),sQuery(id+"F6.wireOp",EDGE,"E21.0"),sQuery(id+"F6.wireOp",EDGE,"E22.0"),sQuery(id+"F6.wireOp",EDGE,"E23.0"),sQuery(id+"F6.wireOp",EDGE,"E24.0")])],"isStart":false})]});
            var Q21;
            Q21=makeQuery(id+"F7.boolean.opBoolean","INTERSECT",EDGE,{"derivedFrom":[makeQuery(id+"F1.opExtrude","SWEPT_FACE",FACE,{"disambiguationData":[OSD([sQuery(id+"F0.wireOp",EDGE,"E0.sketch_text.stroke-80")])]}),makeQuery(id+"F7.opExtrude","CAP_FACE",FACE,{"disambiguationData":[OSD([sQuery(id+"F6.wireOp",EDGE,"E13.0"),sQuery(id+"F6.wireOp",EDGE,"E14.0"),sQuery(id+"F6.wireOp",EDGE,"E15.0"),sQuery(id+"F6.wireOp",EDGE,"E16.0"),sQuery(id+"F6.wireOp",EDGE,"E17.0"),sQuery(id+"F6.wireOp",EDGE,"E18.0"),sQuery(id+"F6.wireOp",EDGE,"E19.0"),sQuery(id+"F6.wireOp",EDGE,"E20.0"),sQuery(id+"F6.wireOp",EDGE,"E21.0"),sQuery(id+"F6.wireOp",EDGE,"E22.0"),sQuery(id+"F6.wireOp",EDGE,"E23.0"),sQuery(id+"F6.wireOp",EDGE,"E24.0")])],"isStart":false})]});
            var Q22;
            Q22=makeQuery(id+"F7.boolean.opBoolean","INTERSECT",EDGE,{"derivedFrom":[makeQuery(id+"F1.opExtrude","SWEPT_FACE",FACE,{"disambiguationData":[OSD([sQuery(id+"F0.wireOp",EDGE,"E0.sketch_text.stroke-71")])]}),makeQuery(id+"F7.opExtrude","CAP_FACE",FACE,{"disambiguationData":[OSD([sQuery(id+"F6.wireOp",EDGE,"E13.0"),sQuery(id+"F6.wireOp",EDGE,"E14.0"),sQuery(id+"F6.wireOp",EDGE,"E15.0"),sQuery(id+"F6.wireOp",EDGE,"E16.0"),sQuery(id+"F6.wireOp",EDGE,"E17.0"),sQuery(id+"F6.wireOp",EDGE,"E18.0"),sQuery(id+"F6.wireOp",EDGE,"E19.0"),sQuery(id+"F6.wireOp",EDGE,"E20.0"),sQuery(id+"F6.wireOp",EDGE,"E21.0"),sQuery(id+"F6.wireOp",EDGE,"E22.0"),sQuery(id+"F6.wireOp",EDGE,"E23.0"),sQuery(id+"F6.wireOp",EDGE,"E24.0")])],"isStart":false})]});
            var Q23;
            Q23=makeQuery(id+"F7.boolean.opBoolean","INTERSECT",EDGE,{"derivedFrom":[makeQuery(id+"F1.opExtrude","SWEPT_FACE",FACE,{"disambiguationData":[OSD([sQuery(id+"F0.wireOp",EDGE,"E0.sketch_text.stroke-91")])]}),makeQuery(id+"F7.opExtrude","CAP_FACE",FACE,{"disambiguationData":[OSD([sQuery(id+"F6.wireOp",EDGE,"E13.0"),sQuery(id+"F6.wireOp",EDGE,"E14.0"),sQuery(id+"F6.wireOp",EDGE,"E15.0"),sQuery(id+"F6.wireOp",EDGE,"E16.0"),sQuery(id+"F6.wireOp",EDGE,"E17.0"),sQuery(id+"F6.wireOp",EDGE,"E18.0"),sQuery(id+"F6.wireOp",EDGE,"E19.0"),sQuery(id+"F6.wireOp",EDGE,"E20.0"),sQuery(id+"F6.wireOp",EDGE,"E21.0"),sQuery(id+"F6.wireOp",EDGE,"E22.0"),sQuery(id+"F6.wireOp",EDGE,"E23.0"),sQuery(id+"F6.wireOp",EDGE,"E24.0")])],"isStart":false})]});
            var Q24;
            Q24=makeQuery(id+"F7.boolean.opBoolean","INTERSECT",EDGE,{"derivedFrom":[makeQuery(id+"F1.opExtrude","SWEPT_FACE",FACE,{"disambiguationData":[OSD([sQuery(id+"F0.wireOp",EDGE,"E0.sketch_text.stroke-90")])]}),makeQuery(id+"F7.opExtrude","CAP_FACE",FACE,{"disambiguationData":[OSD([sQuery(id+"F6.wireOp",EDGE,"E13.0"),sQuery(id+"F6.wireOp",EDGE,"E14.0"),sQuery(id+"F6.wireOp",EDGE,"E15.0"),sQuery(id+"F6.wireOp",EDGE,"E16.0"),sQuery(id+"F6.wireOp",EDGE,"E17.0"),sQuery(id+"F6.wireOp",EDGE,"E18.0"),sQuery(id+"F6.wireOp",EDGE,"E19.0"),sQuery(id+"F6.wireOp",EDGE,"E20.0"),sQuery(id+"F6.wireOp",EDGE,"E21.0"),sQuery(id+"F6.wireOp",EDGE,"E22.0"),sQuery(id+"F6.wireOp",EDGE,"E23.0"),sQuery(id+"F6.wireOp",EDGE,"E24.0")])],"isStart":false})]});
            var Q25;
            Q25=makeQuery(id+"F7.boolean.opBoolean","INTERSECT",EDGE,{"derivedFrom":[makeQuery(id+"F1.opExtrude","SWEPT_FACE",FACE,{"disambiguationData":[OSD([sQuery(id+"F0.wireOp",EDGE,"E0.sketch_text.stroke-87")])]}),makeQuery(id+"F7.opExtrude","CAP_FACE",FACE,{"disambiguationData":[OSD([sQuery(id+"F6.wireOp",EDGE,"E13.0"),sQuery(id+"F6.wireOp",EDGE,"E14.0"),sQuery(id+"F6.wireOp",EDGE,"E15.0"),sQuery(id+"F6.wireOp",EDGE,"E16.0"),sQuery(id+"F6.wireOp",EDGE,"E17.0"),sQuery(id+"F6.wireOp",EDGE,"E18.0"),sQuery(id+"F6.wireOp",EDGE,"E19.0"),sQuery(id+"F6.wireOp",EDGE,"E20.0"),sQuery(id+"F6.wireOp",EDGE,"E21.0"),sQuery(id+"F6.wireOp",EDGE,"E22.0"),sQuery(id+"F6.wireOp",EDGE,"E23.0"),sQuery(id+"F6.wireOp",EDGE,"E24.0")])],"isStart":false})]});
            var Q26;
            Q26=makeQuery(id+"F7.boolean.opBoolean","INTERSECT",EDGE,{"derivedFrom":[makeQuery(id+"F1.opExtrude","SWEPT_FACE",FACE,{"disambiguationData":[OSD([sQuery(id+"F0.wireOp",EDGE,"E0.sketch_text.stroke-85")])]}),makeQuery(id+"F7.opExtrude","CAP_FACE",FACE,{"disambiguationData":[OSD([sQuery(id+"F6.wireOp",EDGE,"E13.0"),sQuery(id+"F6.wireOp",EDGE,"E14.0"),sQuery(id+"F6.wireOp",EDGE,"E15.0"),sQuery(id+"F6.wireOp",EDGE,"E16.0"),sQuery(id+"F6.wireOp",EDGE,"E17.0"),sQuery(id+"F6.wireOp",EDGE,"E18.0"),sQuery(id+"F6.wireOp",EDGE,"E19.0"),sQuery(id+"F6.wireOp",EDGE,"E20.0"),sQuery(id+"F6.wireOp",EDGE,"E21.0"),sQuery(id+"F6.wireOp",EDGE,"E22.0"),sQuery(id+"F6.wireOp",EDGE,"E23.0"),sQuery(id+"F6.wireOp",EDGE,"E24.0")])],"isStart":false})]});
            var Q27;
            Q27=makeQuery(id+"F7.boolean.opBoolean","INTERSECT",EDGE,{"derivedFrom":[makeQuery(id+"F1.opExtrude","SWEPT_FACE",FACE,{"disambiguationData":[OSD([sQuery(id+"F0.wireOp",EDGE,"E0.sketch_text.stroke-96")])]}),makeQuery(id+"F7.opExtrude","CAP_FACE",FACE,{"disambiguationData":[OSD([sQuery(id+"F6.wireOp",EDGE,"E13.0"),sQuery(id+"F6.wireOp",EDGE,"E14.0"),sQuery(id+"F6.wireOp",EDGE,"E15.0"),sQuery(id+"F6.wireOp",EDGE,"E16.0"),sQuery(id+"F6.wireOp",EDGE,"E17.0"),sQuery(id+"F6.wireOp",EDGE,"E18.0"),sQuery(id+"F6.wireOp",EDGE,"E19.0"),sQuery(id+"F6.wireOp",EDGE,"E20.0"),sQuery(id+"F6.wireOp",EDGE,"E21.0"),sQuery(id+"F6.wireOp",EDGE,"E22.0"),sQuery(id+"F6.wireOp",EDGE,"E23.0"),sQuery(id+"F6.wireOp",EDGE,"E24.0")])],"isStart":false})]});
            var Q28;
            Q28=makeQuery(id+"F7.boolean.opBoolean","INTERSECT",EDGE,{"derivedFrom":[makeQuery(id+"F1.opExtrude","SWEPT_FACE",FACE,{"disambiguationData":[OSD([sQuery(id+"F0.wireOp",EDGE,"E0.sketch_text.stroke-92")])]}),makeQuery(id+"F7.opExtrude","CAP_FACE",FACE,{"disambiguationData":[OSD([sQuery(id+"F6.wireOp",EDGE,"E13.0"),sQuery(id+"F6.wireOp",EDGE,"E14.0"),sQuery(id+"F6.wireOp",EDGE,"E15.0"),sQuery(id+"F6.wireOp",EDGE,"E16.0"),sQuery(id+"F6.wireOp",EDGE,"E17.0"),sQuery(id+"F6.wireOp",EDGE,"E18.0"),sQuery(id+"F6.wireOp",EDGE,"E19.0"),sQuery(id+"F6.wireOp",EDGE,"E20.0"),sQuery(id+"F6.wireOp",EDGE,"E21.0"),sQuery(id+"F6.wireOp",EDGE,"E22.0"),sQuery(id+"F6.wireOp",EDGE,"E23.0"),sQuery(id+"F6.wireOp",EDGE,"E24.0")])],"isStart":false})]});
            var Q29;
            Q29=makeQuery(id+"F7.boolean.opBoolean","INTERSECT",EDGE,{"derivedFrom":[makeQuery(id+"F1.opExtrude","SWEPT_FACE",FACE,{"disambiguationData":[OSD([sQuery(id+"F0.wireOp",EDGE,"E0.sketch_text.stroke-93")])]}),makeQuery(id+"F7.opExtrude","CAP_FACE",FACE,{"disambiguationData":[OSD([sQuery(id+"F6.wireOp",EDGE,"E13.0"),sQuery(id+"F6.wireOp",EDGE,"E14.0"),sQuery(id+"F6.wireOp",EDGE,"E15.0"),sQuery(id+"F6.wireOp",EDGE,"E16.0"),sQuery(id+"F6.wireOp",EDGE,"E17.0"),sQuery(id+"F6.wireOp",EDGE,"E18.0"),sQuery(id+"F6.wireOp",EDGE,"E19.0"),sQuery(id+"F6.wireOp",EDGE,"E20.0"),sQuery(id+"F6.wireOp",EDGE,"E21.0"),sQuery(id+"F6.wireOp",EDGE,"E22.0"),sQuery(id+"F6.wireOp",EDGE,"E23.0"),sQuery(id+"F6.wireOp",EDGE,"E24.0")])],"isStart":false})]});
            fillet(context, id + "F10", {"entities" : qUnion([Q0, Q1, Q2, Q3, Q4, Q5, Q6, Q7, Q8, Q9, Q10, Q11, Q12, Q13, Q14, Q15, Q16, Q17, Q18, Q19, Q20, Q21, Q22, Q23, Q24, Q25, Q26, Q27, Q28, Q29]), "radius" : 0.8 * mm, "tangentPropagation" : true, "allowEdgeOverflow" : false});
        }
        {
            var Q0;
            Q0=makeQuery(id+"F7.boolean.opBoolean","SPLIT",FACE,{"disambiguationData":[TD([makeQuery(id+"F1.opExtrude","SWEPT_FACE",FACE,{"disambiguationData":[OSD([sQuery(id+"F0.wireOp",EDGE,"E0.sketch_text.stroke-0")])]})])],"derivedFrom":makeQuery(id+"F7.opExtrude","CAP_FACE",FACE,{"disambiguationData":[OSD([sQuery(id+"F6.wireOp",EDGE,"E13.0"),sQuery(id+"F6.wireOp",EDGE,"E14.0"),sQuery(id+"F6.wireOp",EDGE,"E15.0"),sQuery(id+"F6.wireOp",EDGE,"E16.0"),sQuery(id+"F6.wireOp",EDGE,"E17.0"),sQuery(id+"F6.wireOp",EDGE,"E18.0"),sQuery(id+"F6.wireOp",EDGE,"E19.0"),sQuery(id+"F6.wireOp",EDGE,"E20.0"),sQuery(id+"F6.wireOp",EDGE,"E21.0"),sQuery(id+"F6.wireOp",EDGE,"E22.0"),sQuery(id+"F6.wireOp",EDGE,"E23.0"),sQuery(id+"F6.wireOp",EDGE,"E24.0")])],"isStart":false})});
            var sketch = newSketch(context, id + "F11", { "sketchPlane" : qUnion([Q0])});
            skCircle(sketch, "E29", {"center": v(-6.35, 19.05) * mm, "radius": 6.35 * mm});
            skCircle(sketch, "E30", {"center": v(-6.35, -6.35) * mm, "radius": 6.35 * mm});
            skCircle(sketch, "E31", {"center": v(57.15, 19.05) * mm, "radius": 6.35 * mm});
            skCircle(sketch, "E32", {"center": v(57.15, -6.35) * mm, "radius": 6.35 * mm});
            skSolve(sketch);
        }
        {
            var Q0;
            Q0=qSketchRegion(id+"F11",true);
            extrude(context, id + "F12", {"entities" : qUnion([Q0]), "operationType" : NewBodyOperationType.REMOVE, "endBound" : BoundingType.THROUGH_ALL, "oppositeDirection" : true, "depth" : 25.4 * mm});
        }
    });
